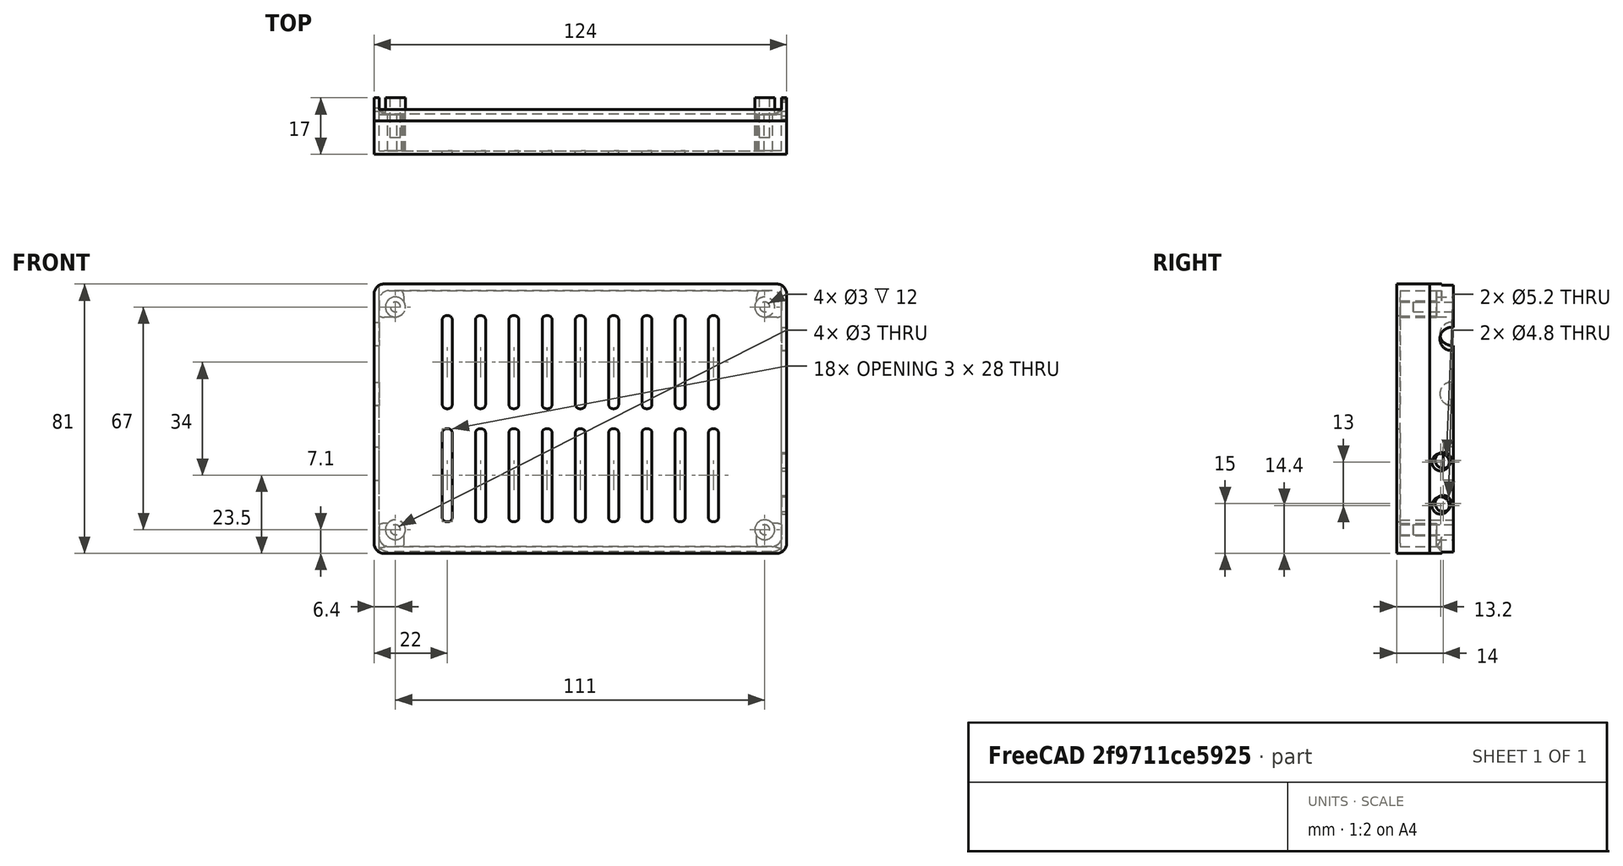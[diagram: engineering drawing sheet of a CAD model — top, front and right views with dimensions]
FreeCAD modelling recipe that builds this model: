
FCSTD DOCUMENT  (FreeCAD 0.18.4R)
Label: hack_rf_one
License: All rights reserved
LicenseURL: http://en.wikipedia.org/wiki/All_rights_reserved
objects: Part::Box×7, Part::FeaturePython×5, Part::Fillet×4, Part::Cylinder×4, Part::MultiFuse×4, Part::Cut×3, Part::Feature×2, PartDesign::FeatureBase×2, PartDesign::Body×2
note: 33 computed .brp shape members not serialized (recipe doc carries the construction recipe); baked Part::Feature solids carry a one-line shape summary decoded from their .brp

FEATURE [Part::Feature] hackrfone_top001
  Placement = pos=(1,1,25) rot=(0,0,1;0rad)
  shape: bbox 125 x 15.03 x 81 mm, 18040 faces, 0 solids (baked)
FEATURE [Part::Box] Box  label="Cube"
  AttacherType = Attacher::AttachEngine3D
  Height = 81
  Length = 124
  Width = 17
FEATURE [Part::Fillet] Fillet
  Base = -> Box
  Edges = 4 edges r=3: [Edge2,Edge4,Edge6,Edge8]
FEATURE [Part::Box] Box001  label="Cube001"
  AttacherType = Attacher::AttachEngine3D
  Height = 77
  Length = 121
  Placement = pos=(1.5,1,2) rot=(0,0,1;0rad)
  Width = 18
FEATURE [Part::Fillet] Fillet001
  Base = -> Box001
  Edges = 4 edges r=3: [Edge2,Edge4,Edge6,Edge8]
FEATURE [Part::Box] Box002  label="Cube002"
  AttacherType = Attacher::AttachEngine3D
  Height = 90
  Length = 121
  Placement = pos=(1.5,13.5,-4) rot=(0,0,1;0rad)
  Width = 3.5
FEATURE [Part::Cylinder] Cylinder  label="ant hole"
  Angle = 360
  AttacherType = Attacher::AttachEngine3D
  Height = 20
  Placement = pos=(-9,13.5,66) rot=(0,1,0;1.5708rad)
  Radius = 3.5
FEATURE [PartDesign::FeatureBase] Clone
  BaseFeature = -> Cylinder
  Placement = pos=(-9,14,66) rot=(0,1,0;1.5708rad)
FEATURE [PartDesign::Body] Body  label="ant hole001"
  BaseFeature = -> Cylinder
  Group = -> [Clone]
  Origin = -> Origin
  Placement = pos=(0,-0.5,-18) rot=(0,0,1;0rad)
  Tip = -> Clone
FEATURE [PartDesign::FeatureBase] Clone001
  BaseFeature = -> Cylinder
  Placement = pos=(-9,14,66) rot=(0,1,0;1.5708rad)
FEATURE [PartDesign::Body] Body001  label="ant hole002"
  BaseFeature = -> Cylinder
  Group = -> [Clone001]
  Origin = -> Origin001
  Placement = pos=(121,-0.5,-1.5) rot=(0,0,1;0rad)
  Tip = -> Clone001
FEATURE [Part::Box] Box003  label="usb cut"
  AttacherType = Attacher::AttachEngine3D
  Height = 10
  Length = 10
  Placement = pos=(-5,11,22) rot=(0,0,1;0rad)
  Width = 4
FEATURE [Part::Cylinder] Cylinder001  label="button hole"
  Angle = 360
  AttacherType = Attacher::AttachEngine3D
  Height = 20
  Placement = pos=(112,10.2,14.4) rot=(0,1,0;1.5708rad)
  Radius = 2.6
FEATURE [Part::FeaturePython] Array  label="button hole array"  # Draft array (typed FeaturePython)
  Angle = 360
  ArrayType = 0
  Axis = (0,0,1)
  Base = -> Cylinder001
  Center = (0,0,0)
  Fuse = false
  IntervalAxis = (0,0,0)
  IntervalX = (1,0,0)
  IntervalY = (0,1,0)
  IntervalZ = (0,0,13)
  NumberPolar = 1
  NumberX = 1
  NumberY = 1
  NumberZ = 2
FEATURE [Part::Cylinder] Cylinder002  label="bolt hole"
  Angle = 360
  AttacherType = Attacher::AttachEngine3D
  Height = 12
  Placement = pos=(6.4,2,7.1) rot=(-1,0,0;1.5708rad)
  Radius = 1.5
FEATURE [Part::FeaturePython] Array001  label="bolt hole array"  # Draft array (typed FeaturePython)
  Angle = 360
  ArrayType = 0
  Axis = (0,0,1)
  Base = -> Cylinder002
  Center = (0,0,0)
  Fuse = false
  IntervalAxis = (0,0,0)
  IntervalX = (111,0,0)
  IntervalY = (0,1,0)
  IntervalZ = (0,0,67)
  NumberPolar = 1
  NumberX = 2
  NumberY = 1
  NumberZ = 2
FEATURE [Part::MultiFuse] Fusion001  label="body extraction fusion"
  Shapes = -> [Fillet001,Box002]
FEATURE [Part::Cut] Cut  label="body cut"
  Base = -> Fillet
  Tool = -> Fusion001
FEATURE [Part::Cylinder] Cylinder003  label="bolt stand"
  Angle = 360
  AttacherType = Attacher::AttachEngine3D
  Height = 16
  Placement = pos=(6.4,1,7.1) rot=(-1,0,0;1.5708rad)
  Radius = 3
FEATURE [Part::FeaturePython] Array002  label="bolt stand array"  # Draft array (typed FeaturePython)
  Angle = 360
  ArrayType = 0
  Axis = (0,0,1)
  Base = -> Cylinder003
  Center = (0,0,0)
  Fuse = false
  IntervalAxis = (0,0,0)
  IntervalX = (111,0,0)
  IntervalY = (0,1,0)
  IntervalZ = (0,0,67)
  NumberPolar = 1
  NumberX = 2
  NumberY = 1
  NumberZ = 2
FEATURE [Part::Box] Box004  label="Cube003"
  AttacherType = Attacher::AttachEngine3D
  Height = 9
  Length = 9
  Width = 12
FEATURE [Part::Fillet] Fillet002
  Base = -> Box004
  Edges = 4 edges r=3: [Edge2,Edge4,Edge6,Edge8]
FEATURE [Part::FeaturePython] Array003  label="bolt stand array001"  # Draft array (typed FeaturePython)
  Angle = 360
  ArrayType = 0
  Axis = (0,0,1)
  Base = -> Fillet002
  Center = (0,0,0)
  Fuse = false
  IntervalAxis = (0,0,0)
  IntervalX = (115,0,0)
  IntervalY = (0,1,0)
  IntervalZ = (0,0,71)
  NumberPolar = 1
  NumberX = 2
  NumberY = 1
  NumberZ = 2
FEATURE [Part::MultiFuse] Fusion  label="bolt stand fusion"
  Shapes = -> [Array002,Array003]
FEATURE [Part::MultiFuse] Fusion003  label="body extra fusion"
  Shapes = -> [Fusion,Cut]
FEATURE [Part::Box] Box005  label="Cube004"
  AttacherType = Attacher::AttachEngine3D
  Height = 100
  Length = 160
  Placement = pos=(0,-8,0) rot=(0,0,1;0rad)
  Width = 18
FEATURE [Part::Feature] Chamfer002
  shape: bbox 145.9 x 20.02 x 103.6 mm, 79 faces (baked)
FEATURE [Part::Cut] Cut003
  Base = -> Chamfer002
  Tool = -> Box005
FEATURE [Part::Box] Box006  label="top hole cube"
  AttacherType = Attacher::AttachEngine3D
  Height = 28
  Length = 3
  Placement = pos=(20.5,0,0) rot=(0,0,1;0rad)
  Width = 10
FEATURE [Part::Fillet] Fillet003  label="top hole cube fillet"
  Base = -> Box006
  Edges = 4 edges r=1.3: [Edge2,Edge4,Edge6,Edge8]
  Placement = pos=(0,0,9.5) rot=(0,0,1;0rad)
FEATURE [Part::FeaturePython] Array004  label="top hole array"  # Draft array (typed FeaturePython)
  Angle = 360
  ArrayType = 0
  Axis = (0,0,1)
  Base = -> Fillet003
  Center = (0,0,0)
  Fuse = false
  IntervalAxis = (0,0,0)
  IntervalX = (10,0,0)
  IntervalY = (0,1,0)
  IntervalZ = (0,0,34)
  NumberPolar = 1
  NumberX = 9
  NumberY = 1
  NumberZ = 2
  Placement = pos=(0,-3,0) rot=(0,0,1;0rad)
FEATURE [Part::MultiFuse] Fusion002  label="hole fusion"
  Placement = pos=(0,3,0) rot=(0,0,1;0rad)
  Shapes = -> [Array,Array001,Box003,Body001,Body,Cylinder,Array004]
FEATURE [Part::Cut] Cut001  label="hackrf box cut"
  Base = -> Fusion003
  Tool = -> Fusion002
